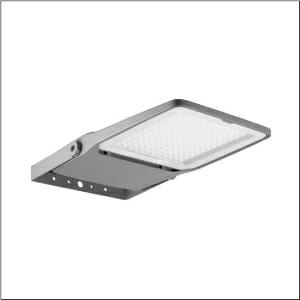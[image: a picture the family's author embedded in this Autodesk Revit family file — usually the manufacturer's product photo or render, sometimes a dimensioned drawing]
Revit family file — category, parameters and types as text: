
# Revit family: floodlight_fl_20_midi___pl43_5xa7682e1a2ac_d3d8
name_source: partatom
category: Lighting Fixtures
units: mm (PartAtom-declared; Revit-internal decimal feet)

## family parameters
Cut with Voids When Loaded = No
Host = Face
Light Source = No
Part Type = Normal
Room Calculation Point = No
Round Connector Dimension = Use Diameter
Shared = No

## types (1)
- --- (1 x LED 3000K / CRI = 80 (unbekannt), 22300 lm, 3000K)
    Apparent Load = 208 VA
    CIE Flux Codes = 32 74 99 100 100
    Color Rendering = 80
    Color Temperature = 3000K
    Default Elevation = 1800 mm
    Description = Floodlight FL 20 midi, floodlight, primary light control with lens, of plastic, primary optical cover: protective disc, of toughened safety glass, transparent, light distribution: PL43, light emission: direct distribution, primary light characteristic: asymmetric, installation type: surface-mounted, LED, High Power LED, rated luminous flux: 22.300lm, luminous efficacy: 107lm/W, light colour: 830, colour temperature: 3000K, control gear: ECG Plus, control: flexible luminous flux parameterisation, time-dependent luminous flux control, digital communication interface, power reduction, overheat protection, electronic power reduction, with terminal, 5-pole, max. 2.5mm², mains connection: 220..240V, AC, 50/60Hz, rated input power: 208W, LED unit, of diecast aluminium, powder-coated, Siteco® metallic grey (DB 702S), corrosivity category C5 mid according to DIN EN ISO 12944, incl. 1x M20 cable gland for cable Ø 6.5..12mm, length: 731mm, width: 450mm, height: 76mm, housing frame, of diecast aluminium, powder-coated, Siteco® metallic grey (DB 702S), wall fastening, of steel, powder-coated, Siteco® metallic grey (DB 702S), DALI, protection rating (complete): IP66, insulation class (complete): insulation class II (safety insulation), certification: CE, ENEC, VDE, protection symbol: D, permissible operating ambient temperature: -40..+40°C, permissible operating ambient temperature for outdoor applications: -40..+50°C, standard: DIN EN 12944, packaging unit: 1 piece

Light Distribution: PL43
    Height = 76 mm
    Lamp = 1 x LED 3000K / CRI >= 80 (unbekannt)
    Lamp Light Flux = 22300 lm
    Lamp count = 1
    Length = 731 mm
    Luminous efficacy = 107 lm/W
    Manufacturer = Siteco
    ModVariant = No
    Model = 5XA7682E1A2AC
    Mounting Place = Wall
    Mounting Type = Surface mounted
    Number of Poles = 1
    OnlyDefault = Yes
    Power Factor = 1
    Product Name = Floodlight FL 20 midi | PL43
    Product group = floodlight | wall mounted
    ProductGroupID = 2001
    Protection Class = Protection class II
    Protection Degree = IP 66
    RLX_Detail_Level = 1
    RLX_Emergency_Light_Flux = 0 lm
    RLX_Emergency_Type = 0
    RLX_Emergency_Type_DB = No
    RlxData = <blob elided: 91973 chars, md5=b7687092>
    Socket = socket
    Standby Power = 0 W
    System Light Flux = 22300 lm
    System Power = 208 W
    Type Comments = factory setting: luminous flux: 100 % | dim-lin: 254 | 484 mA
    Type Image = l_1005944.jpg
    URL = http://relux.com
    VarID = @adj_148403
    Voltage = 0 V
    Weight = 0.00 kg
    Width = 450 mm

## geometry (parser evidence)
native form markers: Blend x4, Sweep x16
no freeform markers — native parametric forms only
